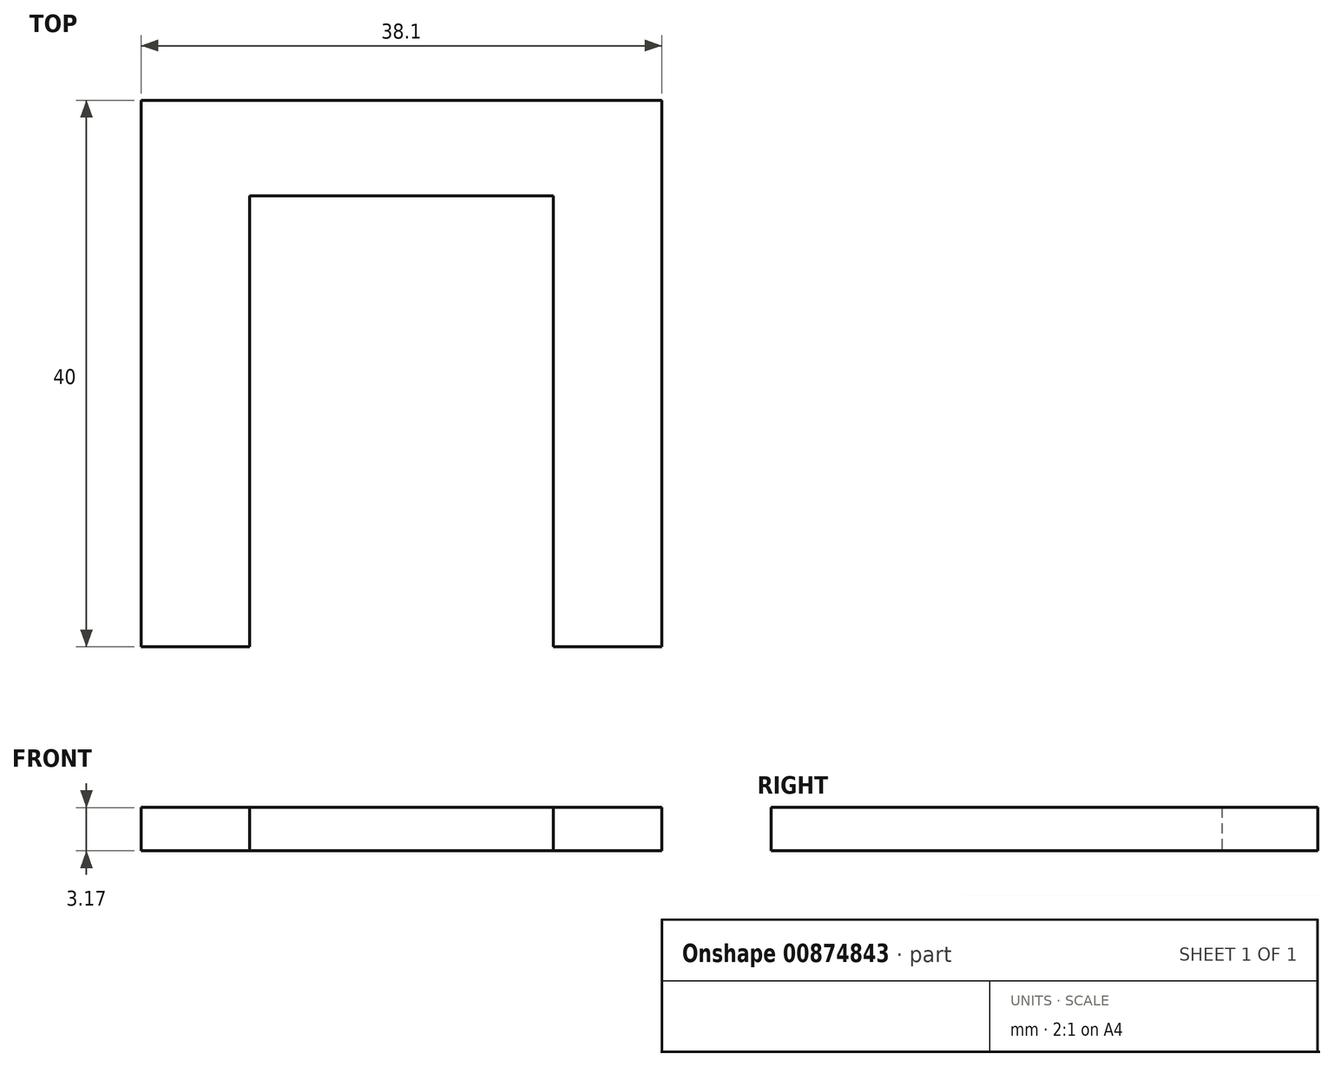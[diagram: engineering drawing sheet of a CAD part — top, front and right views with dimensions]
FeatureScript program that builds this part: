
annotation { "Feature Type Name" : "Feature", "Feature Type Description" : "" }
export const myFeature = defineFeature(function(context is Context, id is Id, definition is map)
    precondition{}
    {
        {
            var Q0;
            Q0=qCreatedBy(makeId("Top.planeOp"),FACE);
            var sketch = newSketch(context, id + "F0", { "sketchPlane" : qUnion([Q0])});
            skLineSegment(sketch, "E0.bottom", {"start": v(-14.96, 21.8) * mm, "end": v(23.14, 21.8) * mm});
            skLineSegment(sketch, "E0.top", {"start": v(-14.96, -18.2) * mm, "end": v(-7.02, -18.2) * mm});
            skLineSegment(sketch, "E0.left", {"start": v(-14.96, 21.8) * mm, "end": v(-14.96, -18.2) * mm});
            skLineSegment(sketch, "E0.right", {"start": v(23.14, 21.8) * mm, "end": v(23.14, -18.2) * mm});
            skLineSegment(sketch, "E1.bottom", {"start": v(-7.02, 14.8) * mm, "end": v(15.2, 14.8) * mm});
            skLineSegment(sketch, "E1.left", {"start": v(-7.02, 14.8) * mm, "end": v(-7.02, -7.25) * mm});
            skLineSegment(sketch, "E1.right", {"start": v(15.2, 14.8) * mm, "end": v(15.2, -7.25) * mm});
            skLineSegment(sketch, "E2", {"start": v(-7.02, -7.25) * mm, "end": v(-7.02, -18.2) * mm});
            skLineSegment(sketch, "E3", {"start": v(15.2, -7.25) * mm, "end": v(15.2, -18.2) * mm});
            skLineSegment(sketch, "E4.trimOffspring", {"start": v(15.2, -18.2) * mm, "end": v(23.14, -18.2) * mm});
            skSolve(sketch);
        }
        {
            var Q0;
            Q0 = qSketchRegion(id + "F0", true);
            extrude(context, id + "F1", {"entities" : qUnion([Q0]), "depth" : 3.17 * mm, "offsetDistance" : 25.4 * mm});
        }
    });
